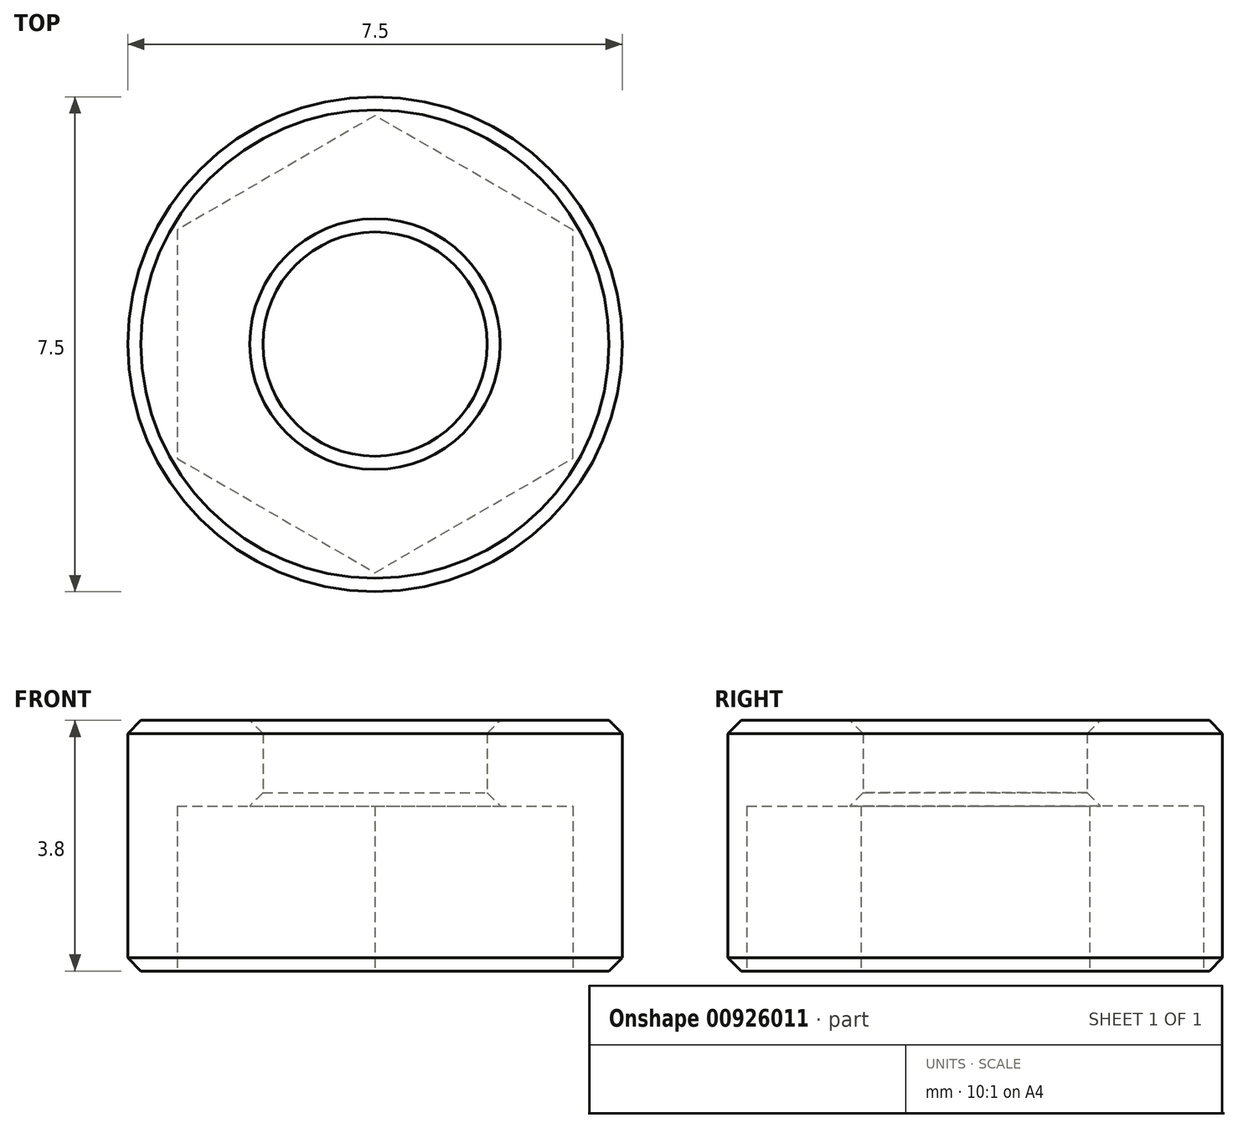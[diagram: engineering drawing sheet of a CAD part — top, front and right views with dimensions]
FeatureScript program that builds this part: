
annotation { "Feature Type Name" : "Feature", "Feature Type Description" : "" }
export const myFeature = defineFeature(function(context is Context, id is Id, definition is map)
    precondition{}
    {
        {
            var Q0;
            Q0=qCreatedBy(makeId("Top.planeOp"),FACE);
            var sketch = newSketch(context, id + "F0", { "sketchPlane" : qUnion([Q0])});
            skCircle(sketch, "E0", {"center": v(56.98, -33.04) * mm, "radius": 3.75 * mm});
            skCircle(sketch, "E1", {"center": v(56.98, -33.04) * mm, "radius": 1.7 * mm});
            skSolve(sketch);
        }
        {
            var Q0;
            Q0=qSketchRegion(id+"F0",true);
            extrude(context, id + "F1", {"entities" : qUnion([Q0]), "depth" : 3.8 * mm, "offsetDistance" : 25 * mm});
        }
        {
            var Q0;
            Q0=makeQuery(id+"F1.opExtrude","CAP_FACE",FACE,{"disambiguationData":[OSD([sQuery(id+"F0.wireOp",EDGE,"E0")])],"isStart":true});
            var sketch = newSketch(context, id + "F2", { "sketchPlane" : qUnion([Q0])});
            skCircle(sketch, "E2.cCircle", {"center": v(56.98, 33.04) * mm, "radius": 3 * mm, "construction": true});
            skLineSegment(sketch, "E2.0", {"start": v(59.98, 34.77) * mm, "end": v(59.98, 31.3) * mm});
            skLineSegment(sketch, "E2.1", {"start": v(59.98, 31.3) * mm, "end": v(56.98, 29.57) * mm});
            skLineSegment(sketch, "E2.2", {"start": v(56.98, 29.57) * mm, "end": v(53.98, 31.3) * mm});
            skLineSegment(sketch, "E2.3", {"start": v(53.98, 31.3) * mm, "end": v(53.98, 34.77) * mm});
            skLineSegment(sketch, "E2.4", {"start": v(53.98, 34.77) * mm, "end": v(56.98, 36.5) * mm});
            skLineSegment(sketch, "E2.5", {"start": v(56.98, 36.5) * mm, "end": v(59.98, 34.77) * mm});
            skPoint(sketch, "E2.0.midPoint", {"position": v(59.98, 33.04) * mm});
            skSolve(sketch);
        }
        {
            var Q0;
            Q0=qSketchRegion(id+"F2",true);
            extrude(context, id + "F3", {"entities" : qUnion([Q0]), "operationType" : NewBodyOperationType.REMOVE, "oppositeDirection" : true, "depth" : 2.5 * mm, "offsetDistance" : 25 * mm});
        }
        {
            var Q0;
            Q0=makeQuery(id+"F1.opExtrude","CAP_EDGE",EDGE,{"disambiguationData":[OSD([sQuery(id+"F0.wireOp",EDGE,"E0")])],"isStart":true});
            var Q1;
            Q1=makeQuery(id+"F1.opExtrude","CAP_EDGE",EDGE,{"disambiguationData":[OSD([sQuery(id+"F0.wireOp",EDGE,"E0")])],"isStart":false});
            var Q2;
            Q2=makeQuery(id+"F1.opExtrude","CAP_EDGE",EDGE,{"disambiguationData":[OSD([sQuery(id+"F0.wireOp",EDGE,"E1")])],"isStart":false});
            var Q3;
            Q3=makeQuery(id+"F3.boolean.opBoolean","INTERSECT",EDGE,{"derivedFrom":[makeQuery(id+"F1.opExtrude","SWEPT_FACE",FACE,{"disambiguationData":[OSD([sQuery(id+"F0.wireOp",EDGE,"E1")])]}),makeQuery(id+"F3.opExtrude","CAP_FACE",FACE,{"disambiguationData":[OSD([sQuery(id+"F2.wireOp",EDGE,"E2.0"),sQuery(id+"F2.wireOp",EDGE,"E2.1"),sQuery(id+"F2.wireOp",EDGE,"E2.2"),sQuery(id+"F2.wireOp",EDGE,"E2.3"),sQuery(id+"F2.wireOp",EDGE,"E2.4"),sQuery(id+"F2.wireOp",EDGE,"E2.5")])],"isStart":false})]});
            var Q4;
            Q4=makeQuery(id+"F3.boolean.opBoolean","COPY",EDGE,{"derivedFrom":makeQuery(id+"F3.opExtrude","CAP_EDGE",EDGE,{"disambiguationData":[OSD([sQuery(id+"F2.wireOp",EDGE,"E2.5")])],"isStart":true})});
            var Q5;
            Q5=makeQuery(id+"F3.boolean.opBoolean","COPY",EDGE,{"derivedFrom":makeQuery(id+"F3.opExtrude","CAP_EDGE",EDGE,{"disambiguationData":[OSD([sQuery(id+"F2.wireOp",EDGE,"E2.0")])],"isStart":true})});
            var Q6;
            Q6=makeQuery(id+"F3.boolean.opBoolean","COPY",EDGE,{"derivedFrom":makeQuery(id+"F3.opExtrude","CAP_EDGE",EDGE,{"disambiguationData":[OSD([sQuery(id+"F2.wireOp",EDGE,"E2.1")])],"isStart":true})});
            var Q7;
            Q7=makeQuery(id+"F3.boolean.opBoolean","COPY",EDGE,{"derivedFrom":makeQuery(id+"F3.opExtrude","CAP_EDGE",EDGE,{"disambiguationData":[OSD([sQuery(id+"F2.wireOp",EDGE,"E2.2")])],"isStart":true})});
            var Q8;
            Q8=makeQuery(id+"F3.boolean.opBoolean","COPY",EDGE,{"derivedFrom":makeQuery(id+"F3.opExtrude","CAP_EDGE",EDGE,{"disambiguationData":[OSD([sQuery(id+"F2.wireOp",EDGE,"E2.3")])],"isStart":true})});
            var Q9;
            Q9=makeQuery(id+"F3.boolean.opBoolean","COPY",EDGE,{"derivedFrom":makeQuery(id+"F3.opExtrude","CAP_EDGE",EDGE,{"disambiguationData":[OSD([sQuery(id+"F2.wireOp",EDGE,"E2.4")])],"isStart":true})});
            chamfer(context, id + "F4", {"entities" : qUnion([Q0, Q1, Q2, Q3, Q4, Q5, Q6, Q7, Q8, Q9]), "width" : 0.2 * mm, "tangentPropagation" : true});
        }
    });
